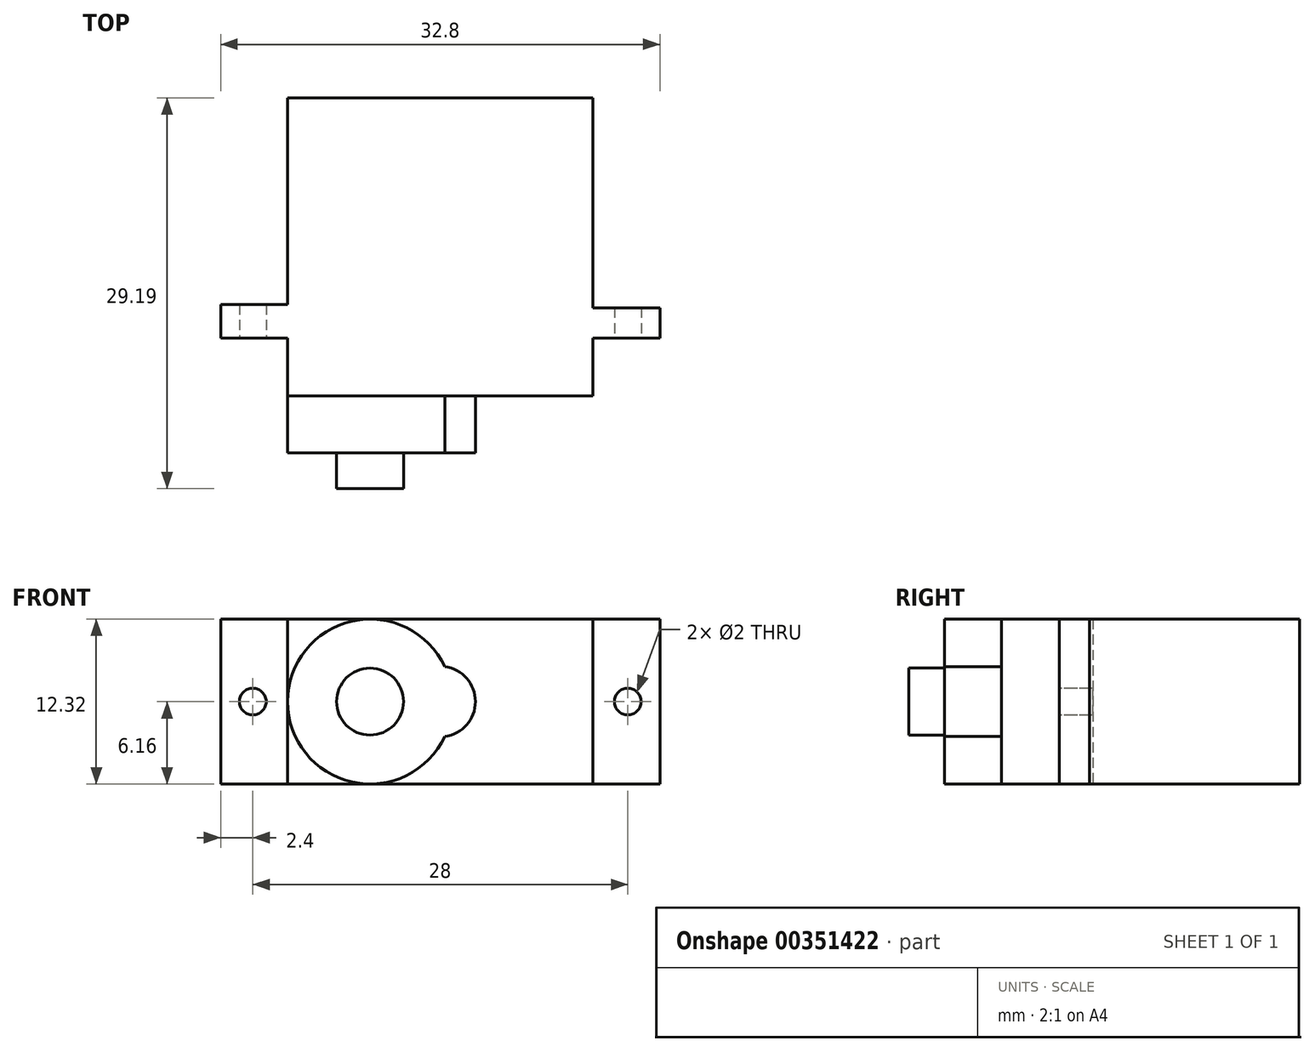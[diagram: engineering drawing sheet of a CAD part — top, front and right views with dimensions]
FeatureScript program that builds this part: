
annotation { "Feature Type Name" : "Feature", "Feature Type Description" : "" }
export const myFeature = defineFeature(function(context is Context, id is Id, definition is map)
    precondition{}
    {
        {
            var Q0;
            Q0=qCreatedBy(makeId("Front.planeOp"),FACE);
            var sketch = newSketch(context, id + "F0", { "sketchPlane" : qUnion([Q0])});
            skLineSegment(sketch, "E0.bottom", {"start": v(11.4, 6.16) * mm, "end": v(-11.4, 6.16) * mm});
            skLineSegment(sketch, "E0.top", {"start": v(11.4, -6.16) * mm, "end": v(-11.4, -6.16) * mm});
            skLineSegment(sketch, "E0.left", {"start": v(11.4, 6.16) * mm, "end": v(11.4, -6.16) * mm});
            skLineSegment(sketch, "E0.right", {"start": v(-11.4, 6.16) * mm, "end": v(-11.4, -6.16) * mm});
            skPoint(sketch, "E0.middle", {"position": v(0, 0) * mm});
            skSolve(sketch);
        }
        {
            var Q0;
            Q0=qSketchRegion(id+"F0",true);
            extrude(context, id + "F1", {"entities" : qUnion([Q0]), "depth" : 22.26 * mm});
        }
        {
            var Q0;
            Q0=makeQuery(id+"F1.opExtrude","CAP_FACE",FACE,{"disambiguationData":[OSD([sQuery(id+"F0.wireOp",EDGE,"E0.bottom"),sQuery(id+"F0.wireOp",EDGE,"E0.top"),sQuery(id+"F0.wireOp",EDGE,"E0.left"),sQuery(id+"F0.wireOp",EDGE,"E0.right")])],"isStart":false});
            var sketch = newSketch(context, id + "F2", { "sketchPlane" : qUnion([Q0])});
            skCircle(sketch, "E1", {"center": v(-5.25, 0) * mm, "radius": 6.16 * mm});
            skPoint(sketch, "E1.centerSnap0", {"position": v(-11.4, 0) * mm});
            skSolve(sketch);
        }
        {
            var Q0;
            Q0=qSketchRegion(id+"F2",true);
            extrude(context, id + "F3", {"entities" : qUnion([Q0]), "operationType" : NewBodyOperationType.ADD, "depth" : 4.25 * mm});
        }
        {
            var Q0;
            {var subQ0=sQuery(id+"F0.wireOp",EDGE,"E0.left");var subQ1=sQuery(id+"F0.wireOp",EDGE,"E0.top");var subQ2=sQuery(id+"F0.wireOp",EDGE,"E0.bottom");var subQ3=makeQuery(id+"F1.opExtrude","CAP_FACE",FACE,{"disambiguationData":[OSD([subQ2,subQ1,subQ0,sQuery(id+"F0.wireOp",EDGE,"E0.right")])],"isStart":false});Q0=makeQuery(id+"F3.boolean.opBoolean","SPLIT",FACE,{"disambiguationData":[TD([makeQuery(id+"F1.opExtrude","SWEPT_FACE",FACE,{"disambiguationData":[OSD([subQ2])]}),subQ3,makeQuery(id+"F1.opExtrude","SWEPT_FACE",FACE,{"disambiguationData":[OSD([subQ1])]}),makeQuery(id+"F1.opExtrude","SWEPT_FACE",FACE,{"disambiguationData":[OSD([subQ0])]}),makeQuery(id+"F3.opExtrude","SWEPT_FACE",FACE,{"disambiguationData":[OSD([sQuery(id+"F2.wireOp",EDGE,"E1")])]})])],"derivedFrom":subQ3});}
            var sketch = newSketch(context, id + "F4", { "sketchPlane" : qUnion([Q0])});
            skCircle(sketch, "E2", {"center": v(0, 0) * mm, "radius": 2.62 * mm});
            skSolve(sketch);
        }
        {
            var Q0;
            Q0=qSketchRegion(id+"F4",true);
            extrude(context, id + "F5", {"entities" : qUnion([Q0]), "operationType" : NewBodyOperationType.ADD, "depth" : 4.25 * mm});
        }
        {
            var Q0;
            Q0=makeQuery(id+"F1.opExtrude","SWEPT_FACE",FACE,{"disambiguationData":[OSD([sQuery(id+"F0.wireOp",EDGE,"E0.right")])]});
            var sketch = newSketch(context, id + "F6", { "sketchPlane" : qUnion([Q0])});
            skLineSegment(sketch, "E3.bottom", {"start": v(15.44, 6.16) * mm, "end": v(17.94, 6.16) * mm});
            skLineSegment(sketch, "E3.top", {"start": v(15.44, -6.16) * mm, "end": v(17.94, -6.16) * mm});
            skLineSegment(sketch, "E3.left", {"start": v(15.44, 6.16) * mm, "end": v(15.44, -6.16) * mm});
            skLineSegment(sketch, "E3.right", {"start": v(17.94, 6.16) * mm, "end": v(17.94, -6.16) * mm});
            skSolve(sketch);
        }
        {
            var Q0;
            Q0=qSketchRegion(id+"F6",true);
            extrude(context, id + "F7", {"entities" : qUnion([Q0]), "operationType" : NewBodyOperationType.ADD, "depth" : 5 * mm});
        }
        {
            var Q0;
            Q0=makeQuery(id+"F1.opExtrude","SWEPT_FACE",FACE,{"disambiguationData":[OSD([sQuery(id+"F0.wireOp",EDGE,"E0.left")])]});
            var sketch = newSketch(context, id + "F8", { "sketchPlane" : qUnion([Q0])});
            skLineSegment(sketch, "E4.bottom", {"start": v(-17.94, 6.16) * mm, "end": v(-15.7, 6.16) * mm});
            skLineSegment(sketch, "E4.top", {"start": v(-17.94, -6.16) * mm, "end": v(-15.7, -6.16) * mm});
            skLineSegment(sketch, "E4.left", {"start": v(-17.94, 6.16) * mm, "end": v(-17.94, -6.16) * mm});
            skLineSegment(sketch, "E4.right", {"start": v(-15.7, 6.16) * mm, "end": v(-15.7, -6.16) * mm});
            skSolve(sketch);
        }
        {
            var Q0;
            Q0=qSketchRegion(id+"F8",true);
            extrude(context, id + "F9", {"entities" : qUnion([Q0]), "operationType" : NewBodyOperationType.ADD, "depth" : 5 * mm});
        }
        {
            var Q0;
            Q0=makeQuery(id+"F5.boolean.opBoolean","MERGE",FACE,{"derivedFrom":[makeQuery(id+"F3.opExtrude","CAP_FACE",FACE,{"disambiguationData":[OSD([sQuery(id+"F2.wireOp",EDGE,"E1")])],"isStart":false}),makeQuery(id+"F5.opExtrude","CAP_FACE",FACE,{"disambiguationData":[OSD([sQuery(id+"F4.wireOp",EDGE,"E2")])],"isStart":false})]});
            var sketch = newSketch(context, id + "F10", { "sketchPlane" : qUnion([Q0])});
            skCircle(sketch, "E5", {"center": v(-5.25, 0) * mm, "radius": 2.5 * mm});
            skSolve(sketch);
        }
        {
            var Q0;
            Q0=qSketchRegion(id+"F10",true);
            extrude(context, id + "F11", {"entities" : qUnion([Q0]), "operationType" : NewBodyOperationType.ADD, "depth" : 2.68 * mm});
        }
        {
            var Q0;
            Q0=makeQuery(id+"F7.opExtrude","SWEPT_FACE",FACE,{"disambiguationData":[OSD([sQuery(id+"F6.wireOp",EDGE,"E3.right")])]});
            var sketch = newSketch(context, id + "F12", { "sketchPlane" : qUnion([Q0])});
            skCircle(sketch, "E6", {"center": v(-14, 0) * mm, "radius": 1 * mm});
            skCircle(sketch, "E7", {"center": v(14, 0) * mm, "radius": 1 * mm});
            skSolve(sketch);
        }
        {
            var Q0;
            Q0=qSketchRegion(id+"F12",true);
            extrude(context, id + "F13", {"entities" : qUnion([Q0]), "operationType" : NewBodyOperationType.REMOVE, "oppositeDirection" : true, "depth" : 25 * mm});
        }
    });
